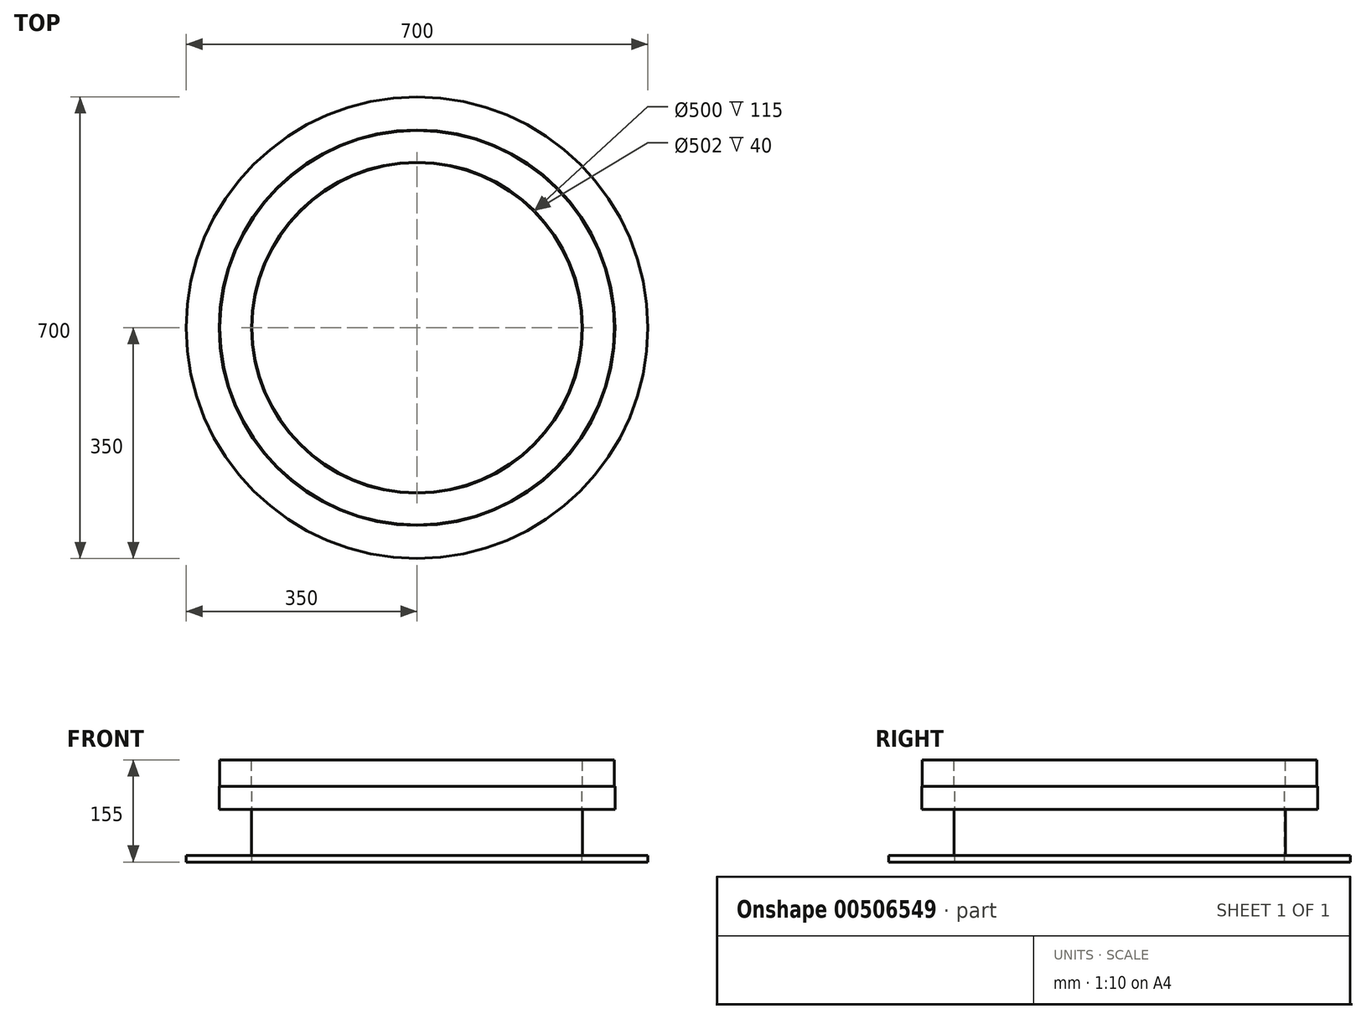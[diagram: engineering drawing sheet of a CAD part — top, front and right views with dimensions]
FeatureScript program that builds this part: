
annotation { "Feature Type Name" : "Feature", "Feature Type Description" : "" }
export const myFeature = defineFeature(function(context is Context, id is Id, definition is map)
    precondition{}
    {
        {
            var Q0;
            Q0=qCreatedBy(makeId("Front.planeOp"),FACE);
            var sketch = newSketch(context, id + "F0", { "sketchPlane" : qUnion([Q0])});
            skLineSegment(sketch, "E0", {"start": v(0, 710.75) * mm, "end": v(0, -704.58) * mm, "construction": true});
            skLineSegment(sketch, "E1", {"start": v(-250, 300.65) * mm, "end": v(-250, 415.65) * mm});
            skLineSegment(sketch, "E2", {"start": v(-250, 415.65) * mm, "end": v(-251, 415.65) * mm});
            skLineSegment(sketch, "E3", {"start": v(-299, 415.65) * mm, "end": v(-300, 415.65) * mm});
            skLineSegment(sketch, "E4", {"start": v(-300, 415.65) * mm, "end": v(-300, 380.65) * mm});
            skLineSegment(sketch, "E5", {"start": v(-300, 380.65) * mm, "end": v(-251, 380.65) * mm});
            skLineSegment(sketch, "E6", {"start": v(-251, 380.65) * mm, "end": v(-251, 310.65) * mm});
            skLineSegment(sketch, "E7", {"start": v(-251, 310.65) * mm, "end": v(-350, 310.65) * mm});
            skLineSegment(sketch, "E8", {"start": v(-350, 310.65) * mm, "end": v(-350, 300.65) * mm});
            skLineSegment(sketch, "E9", {"start": v(-350, 300.65) * mm, "end": v(-250, 300.65) * mm});
            skLineSegment(sketch, "E10", {"start": v(-299, 455.65) * mm, "end": v(-299, 415.65) * mm});
            skLineSegment(sketch, "E11", {"start": v(-299, 455.65) * mm, "end": v(-251, 455.65) * mm});
            skLineSegment(sketch, "E12", {"start": v(-251, 415.65) * mm, "end": v(-251, 455.65) * mm});
            skSolve(sketch);
        }
        {
            var Q0;
            Q0=qSketchRegion(id+"F0",true);
            var Q1;
            Q1=sQuery(id+"F0.wireOp",EDGE,"E0");
            revolve(context, id + "F1", {"entities" : qUnion([Q0]), "axis" : qUnion([Q1]), "revolveType" : RevolveType.FULL});
        }
    });
